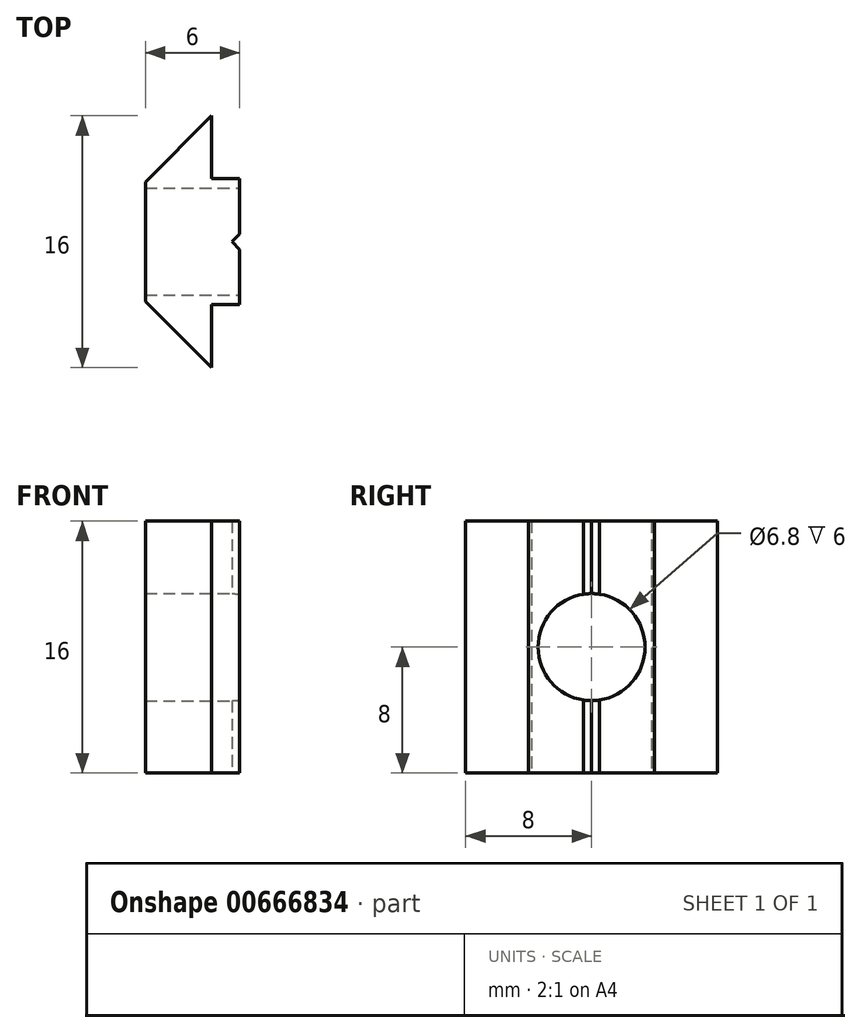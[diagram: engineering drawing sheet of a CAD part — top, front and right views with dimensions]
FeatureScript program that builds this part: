
annotation { "Feature Type Name" : "Feature", "Feature Type Description" : "" }
export const myFeature = defineFeature(function(context is Context, id is Id, definition is map)
    precondition{}
    {
        {
            var Q0;
            Q0=qCreatedBy(makeId("Top.planeOp"),FACE);
            var sketch = newSketch(context, id + "F0", { "sketchPlane" : qUnion([Q0])});
            skLineSegment(sketch, "E0", {"start": v(0, 0.5) * mm, "end": v(0, 4) * mm});
            skLineSegment(sketch, "E1", {"start": v(-6, 0) * mm, "end": v(-6, 3.8) * mm});
            skLineSegment(sketch, "E2", {"start": v(-6, 3.8) * mm, "end": v(-1.8, 8) * mm});
            skLineSegment(sketch, "E3", {"start": v(-1.8, 8) * mm, "end": v(-1.8, 4) * mm});
            skLineSegment(sketch, "E4", {"start": v(0, 4) * mm, "end": v(-1.8, 4) * mm});
            skLineSegment(sketch, "E5.MirrorCS", {"start": v(-6, -3.8) * mm, "end": v(-1.8, -8) * mm});
            skLineSegment(sketch, "E6.MirrorCS", {"start": v(-6, 0) * mm, "end": v(-6, -3.8) * mm});
            skLineSegment(sketch, "E7.MirrorCS", {"start": v(0, -0.5) * mm, "end": v(0, -4) * mm});
            skLineSegment(sketch, "E8.MirrorCS", {"start": v(-1.8, -8) * mm, "end": v(-1.8, -4) * mm});
            skLineSegment(sketch, "E9.MirrorCS", {"start": v(0, -4) * mm, "end": v(-1.8, -4) * mm});
            skLineSegment(sketch, "E10", {"start": v(0, 0.5) * mm, "end": v(-0.5, 0) * mm});
            skLineSegment(sketch, "E11", {"start": v(-0.5, 0) * mm, "end": v(0, -0.5) * mm});
            skPoint(sketch, "E12.orphan", {"position": v(0, 0) * mm});
            skSolve(sketch);
        }
        {
            var Q0;
            Q0 = qSketchRegion(id + "F0", true);
            extrude(context, id + "F1", {"entities" : qUnion([Q0]), "depth" : 16 * mm, "offsetDistance" : 25 * mm});
        }
        {
            var Q0;
            Q0=makeQuery(id+"F1.opExtrude","SWEPT_FACE",FACE,{"disambiguationData":[OSD([sQuery(id+"F0.wireOp",EDGE,"E1"),sQuery(id+"F0.wireOp",EDGE,"E6.MirrorCS")])]});
            var sketch = newSketch(context, id + "F2", { "sketchPlane" : qUnion([Q0])});
            skLineSegment(sketch, "E13", {"start": v(0, 16) * mm, "end": v(0, 0) * mm, "construction": true});
            skPoint(sketch, "E14", {"position": v(0, 8) * mm});
            skSolve(sketch);
        }
        {
            var Q0;
            Q0=sQuery(id+"F2.wireOp",VERTEX,"E14");
            var Q1;
            Q1=makeQuery(id+"F1.opExtrude","SWEPT_BODY",BODY,{"disambiguationData":[OSD([sQuery(id+"F0.wireOp",EDGE,"E0"),sQuery(id+"F0.wireOp",EDGE,"E1"),sQuery(id+"F0.wireOp",EDGE,"E2"),sQuery(id+"F0.wireOp",EDGE,"E3"),sQuery(id+"F0.wireOp",EDGE,"E4"),sQuery(id+"F0.wireOp",EDGE,"E5.MirrorCS"),sQuery(id+"F0.wireOp",EDGE,"E6.MirrorCS"),sQuery(id+"F0.wireOp",EDGE,"E7.MirrorCS"),sQuery(id+"F0.wireOp",EDGE,"E8.MirrorCS"),sQuery(id+"F0.wireOp",EDGE,"E9.MirrorCS"),sQuery(id+"F0.wireOp",EDGE,"E10"),sQuery(id+"F0.wireOp",EDGE,"E11")])]});
            hole(context, id + "F3", {"style" : HoleStyle.SIMPLE, "endStyle" : HoleEndStyle.BLIND, "standardTappedOrClearance" : lookupTablePath({ "standard" : "ISO", "engagement" : "75%", "pitch" : "1.25 mm", "size" : "M8", "type" : "Tapped" }), "standardBlindInLast" : lookupTablePath({ "standard" : "ISO", "fit" : "Normal", "engagement" : "75%", "pitch" : "1.25 mm", "size" : "M8", "type" : "Clearance & tapped" }), "holeDiameter" : 6.8 * mm, "majorDiameter" : 8 * mm, "showTappedDepth" : true, "holeDepth" : 15.75 * mm, "isTappedThrough" : true, "tappedDepth" : 12 * mm, "tapClearance" : 3, "locations" : qUnion([Q0]), "scope" : qUnion([Q1])});
        }
    });
